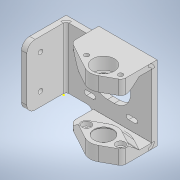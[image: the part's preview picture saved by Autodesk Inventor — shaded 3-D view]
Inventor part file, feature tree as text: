
AUTODESK INVENTOR PART (.ipt)
format: ipt  version: 2022 (Build 260153000, 153)  size: 688,128 bytes
history: native  units: in
note: dims shown in document units (in); Inventor stores cm internally (conversion verified against a paired STEP export)
features: projected_geometry x29, sketch x17, extrude x12, other x7, sheet_metal_op x7, move_body x3, hole x2, chamfer x2, fillet x2, mirror x2, plane x1, boolean_combine x1
ambient origin geometry x8: Origin, YZ Plane, XZ Plane, XY Plane, X Axis, Y Axis, Z Axis, Center Point
bodies: Solid3 (feature_tree), Solid2 (feature_tree)
feature tree (85):
  other  "Z Drive Bearing Holder.ipt"
  sheet_metal_op  "Face1"
  sheet_metal_op  "Flange2"
  sketch  "Sketch3"  dims[d1=2.1654in d4=1.2205in]
  hole  "Hole2"  [1 undecoded]
  sheet_metal_op  "Flange3"
  chamfer  "Corner Round2"
  hole  "Hole3"  [1 undecoded]
  extrude  "Extrusion3"  Depth=1.2205in
  extrude  "Extrusion4"  Depth=0.1969in
  extrude  "Extrusion5"  Depth=0.1969in
  extrude  "Extrusion7"  Depth=0.08in
  extrude  "Extrusion8"  Depth=0.08in
  extrude  "Extrusion9"  Depth=2.4803in
  extrude  "Extrusion10"  Depth=0.4921in
  fillet  "Fillet2"  Radius=1.6929in
  plane  "Work Plane2"
  mirror  "Mirror2"
  move_body  "Move Body2"
  move_body  "Move Body3"
  move_body  "Move Body8"
  boolean_combine  "Combine1"
  extrude  "Extrusion11"  Depth=0.5512in
  extrude  "Extrusion12"  Depth=0.04in
  extrude  "Extrusion15"  Depth=0.08in
  fillet  "Fillet3"  Radius=0.32in
  mirror  "Mirror3"
  extrude  "Extrusion13"  Depth=0.08in
  extrude  "Extrusion16"  Depth=0.3937in
  chamfer  "Chamfer1"  Distance=0.08in
  sketch  "Sketch22"  dims[d98=0.2362in d99=0.08in d100=0.04in d101=0.16in d102=0.08in d103=1.2205in d104=90.0deg d105=0.08in d106=0.32in d107=0.08in d108=0.08in d109=0.3937in d110=0.3937in d111=0.3937in d112=0.1339in d113=0.2362in d114=0.2559in d115=0.1181in d116=0.6181in d117=0.08in d118=0.8108in d119=0.3937in d120=0.0in d121=0.3937in d122=0.0in d123=0.1575in d124=0.3937in d125=0.0in d128=0.3937in d129=0.0in d130=0.0787in d131=0.0in d132=0.1575in d133=0.0787in d134=0.0in d135=0.3937in d136=0.0in d137=0.1969in d138=0.3937in d142=90.0deg d143=90.0deg d156=0.3937in d157=0.0in d158=0.3937in d159=0.0in d160=1.9907in d161=-0.8636in d162=-0.2362in d163=0.3937in d164=0.0in d167=0.4188in d168=0.0in d169=0.1969in d170=0.4188in d171=0.0in d172=0.2555in d173=0.0787in d174=45.0deg]
  other  "Plate1"
  sketch  "Sketch6"  dims[d7=1.2205in d8=1.2205in]
  other  "Plate4"
  sheet_metal_op  "Bend3"
  sheet_metal_op  "Corner2"
  sketch  "Sketch7"  dims[d9=1.2205in d10=1.2205in]
  other  "Plate5"
  sheet_metal_op  "Bend4"
  sheet_metal_op  "Corner3"
  sketch  "Sketch8"  dims[d11=0.0669in d12=0.1969in]
  sketch  "Sketch9"  dims[d13=0.4724in d14=0.1969in]
  projected_geometry  "Projected Loop2"
  projected_geometry  "Projected Loop3"
  sketch  "Sketch10"  dims[d15=0.5906in d16=0.08in]
  projected_geometry  "Projected Loop4"
  sketch  "Sketch11"  dims[d36=0.5512in d41=0.08in]
  projected_geometry  "Projected Loop5"
  projected_geometry  "Projected Loop6"
  projected_geometry  "Projected Loop7"
  projected_geometry  "Projected Loop8"
  sketch  "Sketch12"  dims[d42=0.0in]
  projected_geometry  "Projected Loop9"
  projected_geometry  "Projected Loop10"
  projected_geometry  "Projected Loop11"
  projected_geometry  "Projected Loop12"
  sketch  "Sketch13"  dims[d43=0.1339in d44=0.2362in d45=0.2559in d46=0.1181in d47=90.0deg d48=0.315in d49=0.8108in d53=2.4803in]
  projected_geometry  "Projected Loop13"
  sketch  "Sketch14"  dims[d55=0.4921in d56=0.4921in d83=1.6929in]
  projected_geometry  "Projected Loop14"
  projected_geometry  "Projected Loop15"
  projected_geometry  "Projected Loop16"
  projected_geometry  "Projected Loop17"
  sketch  "Sketch15"  dims[d84=0.1969in d85=0.5512in]
  projected_geometry  "Projected Loop18"
  projected_geometry  "Projected Loop19"
  projected_geometry  "Projected Loop20"
  projected_geometry  "Projected Loop21"
  projected_geometry  "Projected Loop22"
  other  "Solid1::Z Drive Bearing Holder.ipt"
  other  "TaggingFeature1"
  sketch  "Sketch16"  dims[d86=0.08in d87=0.04in]
  projected_geometry  "Projected Loop23"
  sketch  "Sketch17"  dims[d88=0.16in d89=0.08in]
  projected_geometry  "Projected Loop24"
  sketch  "Sketch18"  dims[d90=1.2205in d91=90.0deg d92=0.08in d93=0.32in]
  projected_geometry  "Projected Loop25"
  sketch  "Sketch20"  dims[d94=0.08in d95=0.08in]
  projected_geometry  "Projected Loop27"
  projected_geometry  "Projected Loop28"
  sketch  "Sketch21"  dims[d96=0.3937in d97=0.1575in]
  projected_geometry  "Projected Loop29"
  projected_geometry  "Projected Loop30"
  projected_geometry  "Projected Loop31"
  other  "Cut1"
note: 2 required parameter values undecoded (feature->parameter linkage not recoverable at this tier; creation-order binding heuristic only, values carry confidence <= 0.55)
